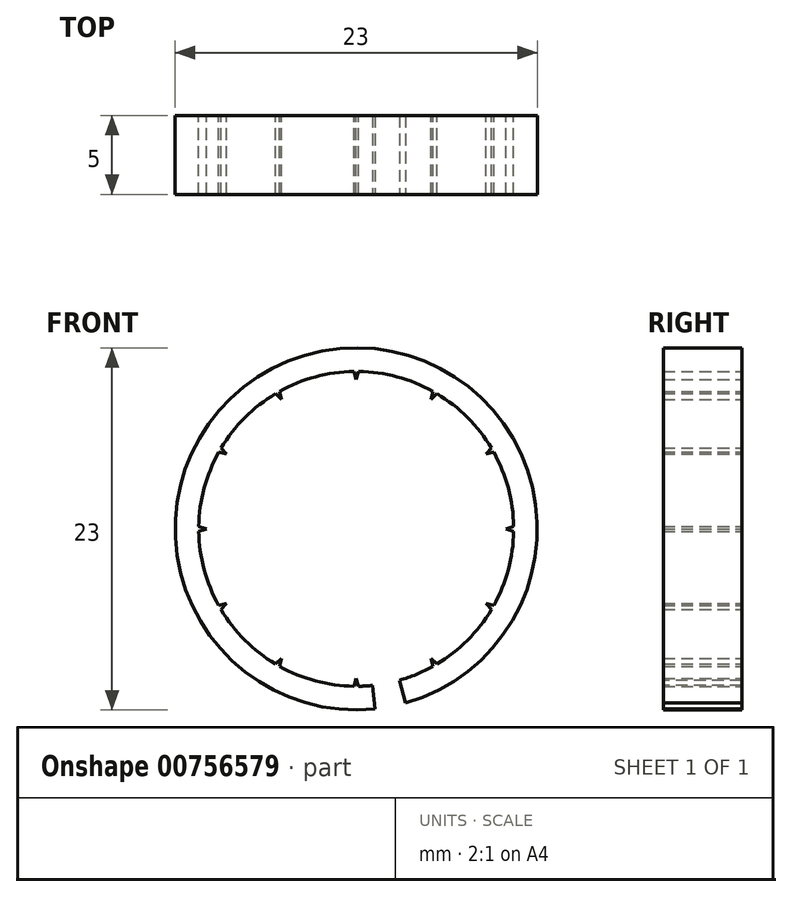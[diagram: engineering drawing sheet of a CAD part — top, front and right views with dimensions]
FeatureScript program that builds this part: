
annotation { "Feature Type Name" : "Feature", "Feature Type Description" : "" }
export const myFeature = defineFeature(function(context is Context, id is Id, definition is map)
    precondition{}
    {
        {
            var Q0;
            Q0=qCreatedBy(makeId("Front.planeOp"),FACE);
            var sketch = newSketch(context, id + "F0", { "sketchPlane" : qUnion([Q0])});
            skCircle(sketch, "E0", {"center": v(0, 0) * mm, "radius": 11.5 * mm});
            skCircle(sketch, "E1", {"center": v(0, 0) * mm, "radius": 9.5 * mm, "construction": true});
            skLineSegment(sketch, "E2", {"start": v(0, 109.46) * mm, "end": v(0, -98.11) * mm, "construction": true});
            skLineSegment(sketch, "E3", {"start": v(-338.44, 0) * mm, "end": v(369.24, 0) * mm, "construction": true});
            skLineSegment(sketch, "E4", {"start": v(-0.15, 10) * mm, "end": v(0, 9.5) * mm});
            skLineSegment(sketch, "E5.MirrorCS", {"start": v(0.15, 10) * mm, "end": v(0, 9.5) * mm});
            skLineSegment(sketch, "E6", {"start": v(0, 0) * mm, "end": v(63.84, 110.57) * mm, "construction": true});
            skArc(sketch, "E7", {"start": v(4.87, 8.73) * mm, "mid": v(2.59, 9.66) * mm, "end": v(0.15, 10) * mm});
            skLineSegment(sketch, "E8.1.0", {"start": v(-5.13, 8.58) * mm, "end": v(-4.75, 8.23) * mm});
            skLineSegment(sketch, "E8.1.1", {"start": v(-4.87, 8.73) * mm, "end": v(-4.75, 8.23) * mm});
            skArc(sketch, "E8.1.2", {"start": v(-0.15, 10) * mm, "mid": v(-2.59, 9.66) * mm, "end": v(-4.87, 8.73) * mm});
            skLineSegment(sketch, "E8.2.0", {"start": v(-8.73, 4.87) * mm, "end": v(-8.23, 4.75) * mm});
            skLineSegment(sketch, "E8.2.1", {"start": v(-8.58, 5.13) * mm, "end": v(-8.23, 4.75) * mm});
            skArc(sketch, "E8.2.2", {"start": v(-5.13, 8.58) * mm, "mid": v(-7.07, 7.07) * mm, "end": v(-8.58, 5.13) * mm});
            skLineSegment(sketch, "E9.2.3.0", {"start": v(-10, -0.15) * mm, "end": v(-9.5, 0) * mm});
            skLineSegment(sketch, "E9.3.3.0", {"start": v(-10, 0.15) * mm, "end": v(-9.5, 0) * mm});
            skArc(sketch, "E9.6.3.0", {"start": v(-8.73, 4.87) * mm, "mid": v(-9.66, 2.59) * mm, "end": v(-10, 0.15) * mm});
            skLineSegment(sketch, "E9.2.4.0", {"start": v(-8.58, -5.13) * mm, "end": v(-8.23, -4.75) * mm});
            skLineSegment(sketch, "E9.3.4.0", {"start": v(-8.73, -4.87) * mm, "end": v(-8.23, -4.75) * mm});
            skArc(sketch, "E9.6.4.0", {"start": v(-10, -0.15) * mm, "mid": v(-9.66, -2.59) * mm, "end": v(-8.73, -4.87) * mm});
            skLineSegment(sketch, "E9.2.5.0", {"start": v(-4.87, -8.73) * mm, "end": v(-4.75, -8.23) * mm});
            skLineSegment(sketch, "E9.3.5.0", {"start": v(-5.13, -8.58) * mm, "end": v(-4.75, -8.23) * mm});
            skArc(sketch, "E9.6.5.0", {"start": v(-8.58, -5.13) * mm, "mid": v(-7.07, -7.07) * mm, "end": v(-5.13, -8.58) * mm});
            skLineSegment(sketch, "E9.2.6.0", {"start": v(0.15, -10) * mm, "end": v(0, -9.5) * mm});
            skLineSegment(sketch, "E9.3.6.0", {"start": v(-0.15, -10) * mm, "end": v(0, -9.5) * mm});
            skArc(sketch, "E9.6.6.0", {"start": v(-4.87, -8.73) * mm, "mid": v(-2.59, -9.66) * mm, "end": v(-0.15, -10) * mm});
            skLineSegment(sketch, "E9.2.7.0", {"start": v(5.13, -8.58) * mm, "end": v(4.75, -8.23) * mm});
            skLineSegment(sketch, "E9.3.7.0", {"start": v(4.87, -8.73) * mm, "end": v(4.75, -8.23) * mm});
            skArc(sketch, "E9.6.7.0", {"start": v(0.15, -10) * mm, "mid": v(2.59, -9.66) * mm, "end": v(4.87, -8.73) * mm});
            skLineSegment(sketch, "E9.2.8.0", {"start": v(8.73, -4.87) * mm, "end": v(8.23, -4.75) * mm});
            skLineSegment(sketch, "E9.3.8.0", {"start": v(8.58, -5.13) * mm, "end": v(8.23, -4.75) * mm});
            skArc(sketch, "E9.6.8.0", {"start": v(5.13, -8.58) * mm, "mid": v(7.07, -7.07) * mm, "end": v(8.58, -5.13) * mm});
            skLineSegment(sketch, "E9.2.9.0", {"start": v(10, 0.15) * mm, "end": v(9.5, 0) * mm});
            skLineSegment(sketch, "E9.3.9.0", {"start": v(10, -0.15) * mm, "end": v(9.5, 0) * mm});
            skArc(sketch, "E9.6.9.0", {"start": v(8.73, -4.87) * mm, "mid": v(9.66, -2.59) * mm, "end": v(10, -0.15) * mm});
            skLineSegment(sketch, "E9.2.10.0", {"start": v(8.58, 5.13) * mm, "end": v(8.23, 4.75) * mm});
            skLineSegment(sketch, "E9.3.10.0", {"start": v(8.73, 4.87) * mm, "end": v(8.23, 4.75) * mm});
            skArc(sketch, "E9.6.10.0", {"start": v(10, 0.15) * mm, "mid": v(9.66, 2.59) * mm, "end": v(8.73, 4.87) * mm});
            skLineSegment(sketch, "E9.2.11.0", {"start": v(4.87, 8.73) * mm, "end": v(4.75, 8.23) * mm});
            skLineSegment(sketch, "E9.3.11.0", {"start": v(5.13, 8.58) * mm, "end": v(4.75, 8.23) * mm});
            skArc(sketch, "E9.6.11.0", {"start": v(8.58, 5.13) * mm, "mid": v(7.07, 7.07) * mm, "end": v(5.13, 8.58) * mm});
            skSolve(sketch);
        }
        {
            var Q0;
            Q0=makeQuery(id+"F0.imprint","IMPRINT",FACE,{"disambiguationData":[TD([[makeQuery(id+"F0.imprint","IMPRINT",EDGE,{"derivedFrom":sQuery(id+"F0.wireOp",EDGE,"E0")}),1.0]])]});
            extrude(context, id + "F1", {"entities" : qUnion([Q0]), "depth" : 5 * mm, "offsetDistance" : 25 * mm});
        }
        {
            var Q0;
            Q0=makeQuery(id+"F1.opExtrude","CAP_FACE",FACE,{"disambiguationData":[OSD([sQuery(id+"F0.wireOp",EDGE,"E0"),sQuery(id+"F0.wireOp",EDGE,"E4"),sQuery(id+"F0.wireOp",EDGE,"E5.MirrorCS"),sQuery(id+"F0.wireOp",EDGE,"E7"),sQuery(id+"F0.wireOp",EDGE,"E8.1.0"),sQuery(id+"F0.wireOp",EDGE,"E8.1.1"),sQuery(id+"F0.wireOp",EDGE,"E8.1.2"),sQuery(id+"F0.wireOp",EDGE,"E8.2.0"),sQuery(id+"F0.wireOp",EDGE,"E8.2.1"),sQuery(id+"F0.wireOp",EDGE,"E8.2.2"),sQuery(id+"F0.wireOp",EDGE,"E9.2.3.0"),sQuery(id+"F0.wireOp",EDGE,"E9.3.3.0"),sQuery(id+"F0.wireOp",EDGE,"E9.6.3.0"),sQuery(id+"F0.wireOp",EDGE,"E9.2.4.0"),sQuery(id+"F0.wireOp",EDGE,"E9.3.4.0"),sQuery(id+"F0.wireOp",EDGE,"E9.6.4.0"),sQuery(id+"F0.wireOp",EDGE,"E9.2.5.0"),sQuery(id+"F0.wireOp",EDGE,"E9.3.5.0"),sQuery(id+"F0.wireOp",EDGE,"E9.6.5.0"),sQuery(id+"F0.wireOp",EDGE,"E9.2.6.0"),sQuery(id+"F0.wireOp",EDGE,"E9.3.6.0"),sQuery(id+"F0.wireOp",EDGE,"E9.6.6.0"),sQuery(id+"F0.wireOp",EDGE,"E9.2.7.0"),sQuery(id+"F0.wireOp",EDGE,"E9.3.7.0"),sQuery(id+"F0.wireOp",EDGE,"E9.6.7.0"),sQuery(id+"F0.wireOp",EDGE,"E9.2.8.0"),sQuery(id+"F0.wireOp",EDGE,"E9.3.8.0"),sQuery(id+"F0.wireOp",EDGE,"E9.6.8.0"),sQuery(id+"F0.wireOp",EDGE,"E9.2.9.0"),sQuery(id+"F0.wireOp",EDGE,"E9.3.9.0"),sQuery(id+"F0.wireOp",EDGE,"E9.6.9.0"),sQuery(id+"F0.wireOp",EDGE,"E9.2.10.0"),sQuery(id+"F0.wireOp",EDGE,"E9.3.10.0"),sQuery(id+"F0.wireOp",EDGE,"E9.6.10.0"),sQuery(id+"F0.wireOp",EDGE,"E9.2.11.0"),sQuery(id+"F0.wireOp",EDGE,"E9.3.11.0"),sQuery(id+"F0.wireOp",EDGE,"E9.6.11.0")])],"isStart":false});
            var sketch = newSketch(context, id + "F2", { "sketchPlane" : qUnion([Q0])});
            skLineSegment(sketch, "E10", {"start": v(0, 0) * mm, "end": v(1.64, -15.88) * mm, "construction": true});
            skLineSegment(sketch, "E11", {"start": v(0, 0) * mm, "end": v(4.44, -15.62) * mm, "construction": true});
            skLineSegment(sketch, "E12", {"start": v(1.02, -9.95) * mm, "end": v(1.18, -11.44) * mm});
            skLineSegment(sketch, "E13", {"start": v(2.73, -9.62) * mm, "end": v(3.14, -11.06) * mm});
            skArc(sketch, "E14.0", {"start": v(1.02, -9.95) * mm, "mid": v(1.89, -9.82) * mm, "end": v(2.73, -9.62) * mm});
            skArc(sketch, "E15.0", {"start": v(1.18, -11.44) * mm, "mid": v(2.17, -11.3) * mm, "end": v(3.14, -11.06) * mm});
            skPoint(sketch, "E16.orphan", {"position": v(0.15, -10) * mm});
            skPoint(sketch, "E17.orphan", {"position": v(4.87, -8.73) * mm});
            skSolve(sketch);
        }
        {
            var Q0;
            Q0 = qSketchRegion(id + "F2", true);
            extrude(context, id + "F3", {"entities" : qUnion([Q0]), "operationType" : NewBodyOperationType.REMOVE, "oppositeDirection" : true, "depth" : 25 * mm, "offsetDistance" : 25 * mm});
        }
    });
